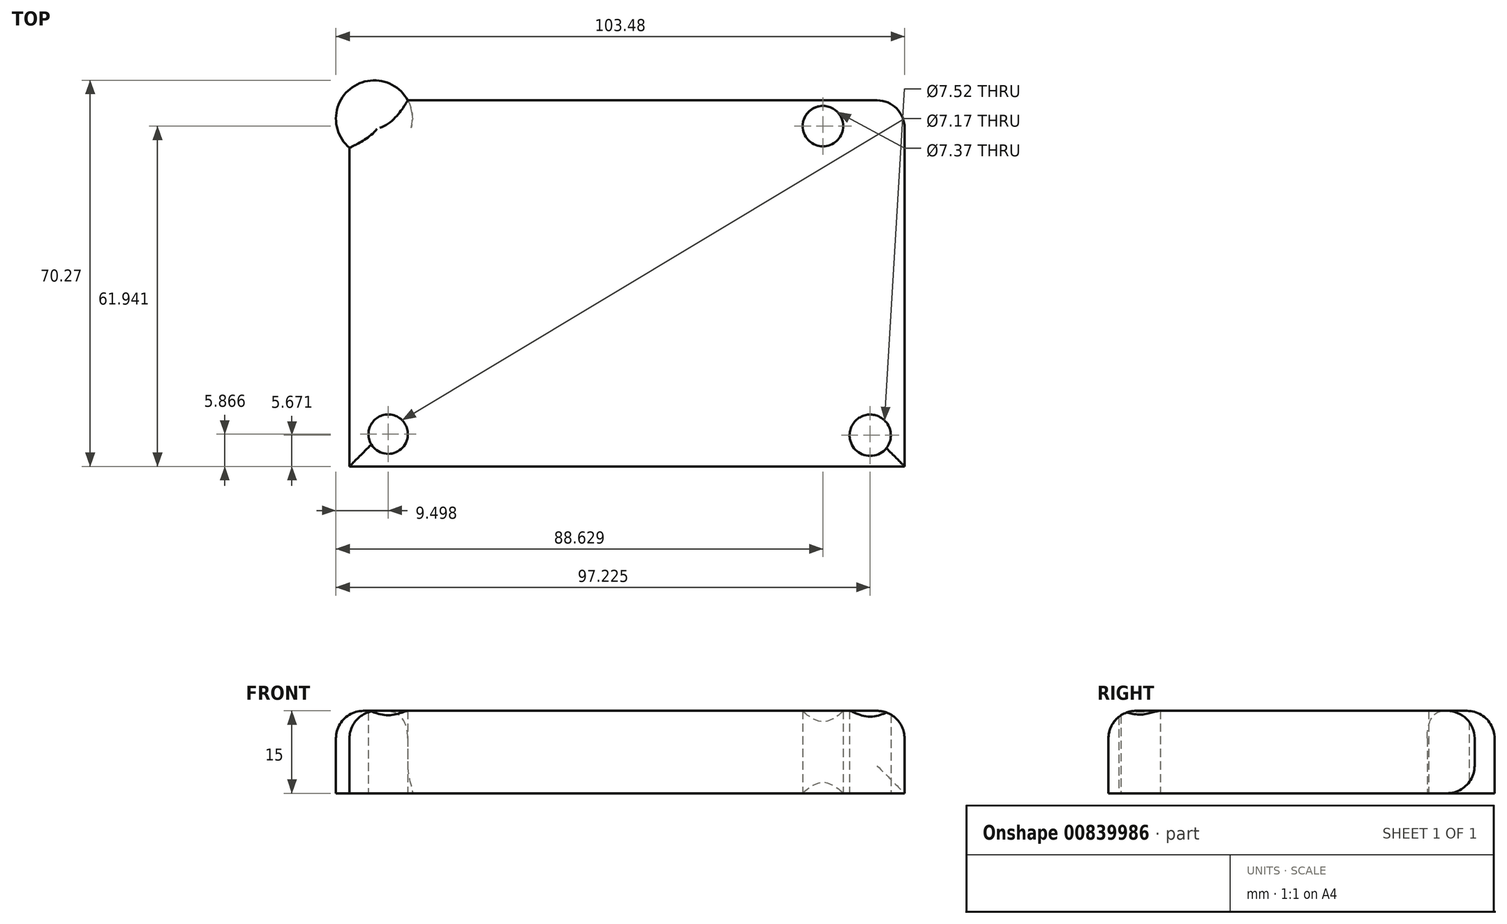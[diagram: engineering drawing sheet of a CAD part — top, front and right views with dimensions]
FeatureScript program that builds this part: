
annotation { "Feature Type Name" : "Feature", "Feature Type Description" : "" }
export const myFeature = defineFeature(function(context is Context, id is Id, definition is map)
    precondition{}
    {
        {
            var Q0;
            Q0=qCreatedBy(makeId("Top.planeOp"),FACE);
            var sketch = newSketch(context, id + "F0", { "sketchPlane" : qUnion([Q0])});
            skLineSegment(sketch, "E0.bottom", {"start": v(-47.58, 30.87) * mm, "end": v(53.44, 30.87) * mm});
            skLineSegment(sketch, "E0.top", {"start": v(-47.58, -35.76) * mm, "end": v(53.44, -35.76) * mm});
            skLineSegment(sketch, "E0.left", {"start": v(-47.58, 30.87) * mm, "end": v(-47.58, -35.76) * mm});
            skLineSegment(sketch, "E0.right", {"start": v(53.44, 30.87) * mm, "end": v(53.44, -35.76) * mm});
            skCircle(sketch, "E1", {"center": v(-43.08, 27.55) * mm, "radius": 6.96 * mm});
            skCircle(sketch, "E2", {"center": v(38.59, 26.18) * mm, "radius": 3.69 * mm});
            skCircle(sketch, "E3", {"center": v(47.19, -30.09) * mm, "radius": 3.76 * mm});
            skCircle(sketch, "E4", {"center": v(-40.54, -29.9) * mm, "radius": 3.59 * mm});
            skSolve(sketch);
        }
        {
            var Q0;
            Q0 = qSketchRegion(id + "F0", true);
            extrude(context, id + "F1", {"entities" : qUnion([Q0]), "depth" : 15 * mm, "offsetDistance" : 25 * mm});
        }
        {
            var Q0;
            Q0=makeQuery(id+"F1.opExtrude","CAP_EDGE",EDGE,{"disambiguationData":[OSD([sQuery(id+"F0.wireOp",EDGE,"E0.top")])],"isStart":false});
            var Q1;
            Q1=makeQuery(id+"F1.opExtrude","CAP_EDGE",EDGE,{"disambiguationData":[OSD([sQuery(id+"F0.wireOp",EDGE,"E0.bottom")])],"isStart":false});
            var Q2;
            Q2=makeQuery(id+"F1.opExtrude","SWEPT_EDGE",EDGE,{"disambiguationData":[OSD([sQuery(id+"F0.wireOp",EDGE,"E0.bottom"),sQuery(id+"F0.wireOp",EDGE,"E0.right")])]});
            var Q3;
            Q3=makeQuery(id+"F1.opExtrude","CAP_EDGE",EDGE,{"disambiguationData":[OSD([sQuery(id+"F0.wireOp",EDGE,"E0.right")])],"isStart":false});
            var Q4;
            Q4=makeQuery(id+"F1.opExtrude","CAP_EDGE",EDGE,{"disambiguationData":[OSD([sQuery(id+"F0.wireOp",EDGE,"E0.left")])],"isStart":false});
            var Q5;
            Q5=makeQuery(id+"F1.opExtrude","CAP_EDGE",EDGE,{"disambiguationData":[OSD([sQuery(id+"F0.wireOp",EDGE,"E1")])],"isStart":false});
            var Q6;
            Q6=makeQuery(id+"F1.opExtrude","CAP_EDGE",EDGE,{"disambiguationData":[OSD([sQuery(id+"F0.wireOp",EDGE,"E0.bottom")])],"isStart":true});
            fillet(context, id + "F2", {"entities" : qUnion([Q0, Q1, Q2, Q3, Q4, Q5, Q6]), "radius" : 5 * mm, "tangentPropagation" : true, "allowEdgeOverflow" : false});
        }
    });
